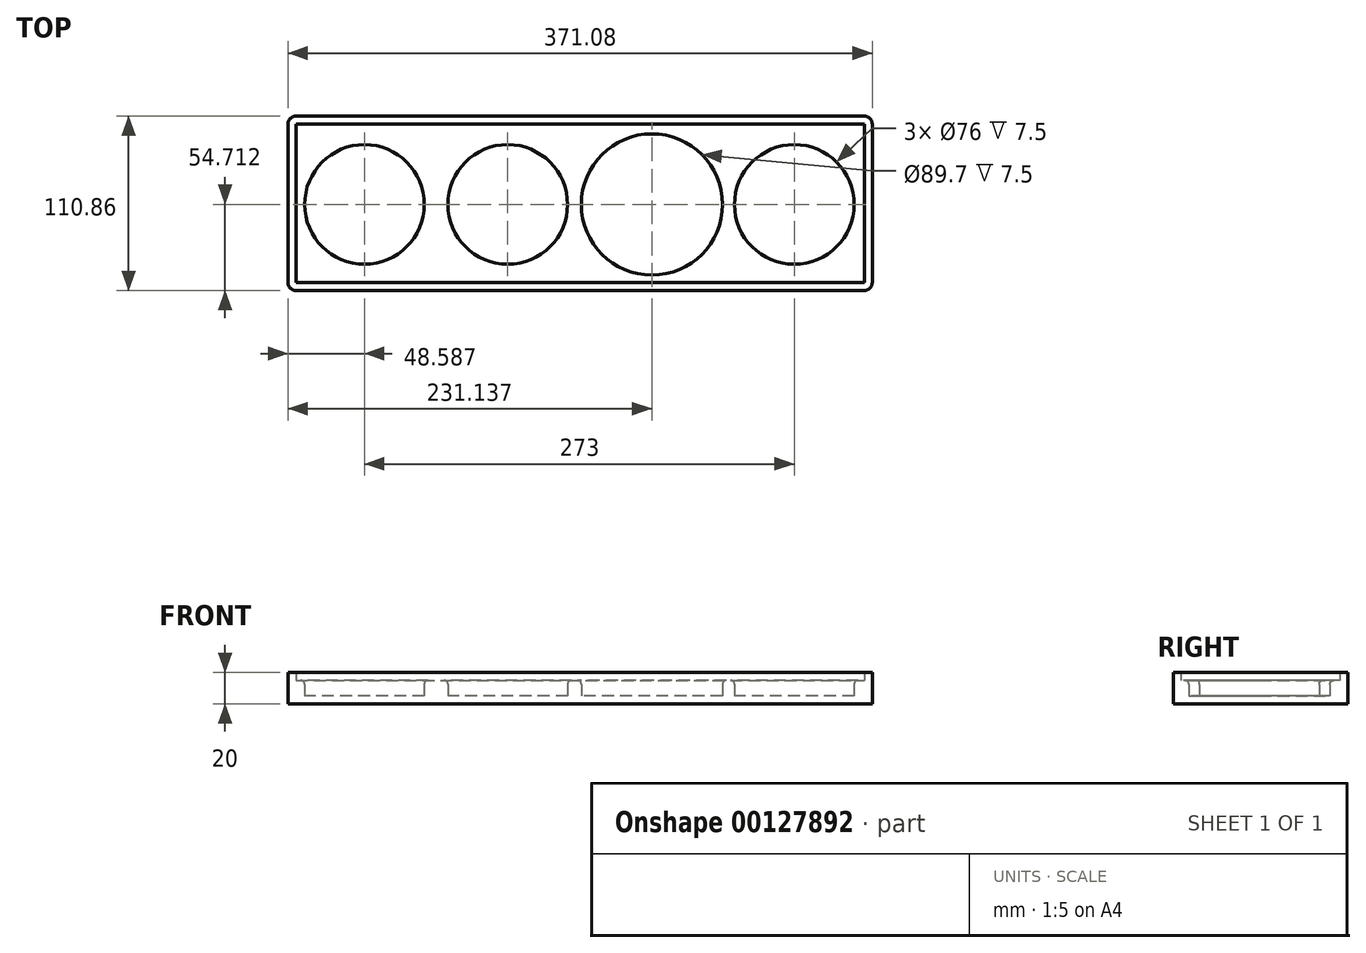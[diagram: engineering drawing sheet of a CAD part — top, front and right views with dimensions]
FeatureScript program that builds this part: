
annotation { "Feature Type Name" : "Feature", "Feature Type Description" : "" }
export const myFeature = defineFeature(function(context is Context, id is Id, definition is map)
    precondition{}
    {
        {
            var Q0;
            Q0=qCreatedBy(makeId("Top.planeOp"),FACE);
            var sketch = newSketch(context, id + "F0", { "sketchPlane" : qUnion([Q0])});
            skCircle(sketch, "E0", {"center": v(-103.8, 10.07) * mm, "radius": 38 * mm});
            skCircle(sketch, "E1.1.0.0", {"center": v(-12.8, 10.07) * mm, "radius": 38 * mm});
            skCircle(sketch, "E1.3.0.0", {"center": v(169.2, 10.07) * mm, "radius": 38 * mm});
            skLineSegment(sketch, "E1.direction1", {"start": v(-103.8, 10.07) * mm, "end": v(-12.8, 10.07) * mm, "construction": true});
            skCircle(sketch, "E2", {"center": v(78.76, 10.07) * mm, "radius": 44.85 * mm});
            skSolve(sketch);
        }
        {
            var Q0;
            Q0=makeQuery(id+"F0.imprint","IMPRINT",FACE,{"disambiguationData":[TD([[makeQuery(id+"F0.imprint","IMPRINT",EDGE,{"derivedFrom":sQuery(id+"F0.wireOp",EDGE,"E0")}),1.0]])]});
            var Q1;
            Q1=makeQuery(id+"F0.imprint","IMPRINT",FACE,{"disambiguationData":[TD([[makeQuery(id+"F0.imprint","IMPRINT",EDGE,{"derivedFrom":sQuery(id+"F0.wireOp",EDGE,"E1.1.0.0")}),1.0]])]});
            var Q2;
            Q2=makeQuery(id+"F0.imprint","IMPRINT",FACE,{"disambiguationData":[TD([[makeQuery(id+"F0.imprint","IMPRINT",EDGE,{"derivedFrom":sQuery(id+"F0.wireOp",EDGE,"E2")}),1.0]])]});
            var Q3;
            Q3=makeQuery(id+"F0.imprint","IMPRINT",FACE,{"disambiguationData":[TD([[makeQuery(id+"F0.imprint","IMPRINT",EDGE,{"derivedFrom":sQuery(id+"F0.wireOp",EDGE,"E1.3.0.0")}),1.0]])]});
            extrude(context, id + "F1", {"entities" : qUnion([Q0, Q1, Q2, Q3]), "depth" : 100 * mm});
        }
        {
            var Q0;
            Q0=qCreatedBy(makeId("Top.planeOp"),FACE);
            var sketch = newSketch(context, id + "F2", { "sketchPlane" : qUnion([Q0])});
            skLineSegment(sketch, "E3.bottom", {"start": v(-148.45, 62.29) * mm, "end": v(214.77, 62.29) * mm});
            skLineSegment(sketch, "E3.top", {"start": v(-148.45, -40.71) * mm, "end": v(214.77, -40.71) * mm});
            skLineSegment(sketch, "E3.left", {"start": v(-148.45, 62.29) * mm, "end": v(-148.45, -40.71) * mm});
            skLineSegment(sketch, "E3.right", {"start": v(214.77, 62.29) * mm, "end": v(214.77, -40.71) * mm});
            skCircle(sketch, "E4.0", {"center": v(78.76, 10.07) * mm, "radius": 44.85 * mm, "construction": true});
            skCircle(sketch, "E5.0", {"center": v(169.2, 10.07) * mm, "radius": 38 * mm, "construction": true});
            skCircle(sketch, "E6.0", {"center": v(-12.8, 10.07) * mm, "radius": 38 * mm, "construction": true});
            skCircle(sketch, "E7.0", {"center": v(-103.8, 10.07) * mm, "radius": 38 * mm, "construction": true});
            skLineSegment(sketch, "E8", {"start": v(169.2, 10.07) * mm, "end": v(214.77, 10.07) * mm, "construction": true});
            skPoint(sketch, "E8.endSnap0", {"position": v(214.77, 10.79) * mm});
            skLineSegment(sketch, "E9.0", {"start": v(-152.38, 66.22) * mm, "end": v(218.7, 66.22) * mm});
            skLineSegment(sketch, "E9.1", {"start": v(-152.38, 66.22) * mm, "end": v(-152.38, -44.64) * mm});
            skLineSegment(sketch, "E9.2", {"start": v(-152.38, -44.64) * mm, "end": v(218.7, -44.64) * mm});
            skLineSegment(sketch, "E9.3", {"start": v(218.7, 66.22) * mm, "end": v(218.7, -44.64) * mm});
            skSolve(sketch);
        }
        {
            var Q0;
            Q0=makeQuery(id+"F2.imprint","IMPRINT",FACE,{"disambiguationData":[TD([[makeQuery(id+"F2.imprint","IMPRINT",EDGE,{"derivedFrom":sQuery(id+"F2.wireOp",EDGE,"E3.bottom")}),-1.0]])]});
            var Q1;
            Q1=makeQuery(id+"F2.imprint","IMPRINT",FACE,{"disambiguationData":[TD([[makeQuery(id+"F2.imprint","IMPRINT",EDGE,{"derivedFrom":sQuery(id+"F2.wireOp",EDGE,"E3.bottom")}),1.0]])]});
            extrude(context, id + "F3", {"entities" : qUnion([Q0, Q1]), "depth" : 15 * mm});
        }
        {
            var Q0;
            Q0=makeQuery(id+"F3.opExtrude","CAP_FACE",FACE,{"disambiguationData":[OSD([sQuery(id+"F2.wireOp",EDGE,"E9.0"),sQuery(id+"F2.wireOp",EDGE,"E9.1"),sQuery(id+"F2.wireOp",EDGE,"E9.2"),sQuery(id+"F2.wireOp",EDGE,"E9.3")])],"isStart":false});
            var sketch = newSketch(context, id + "F4", { "sketchPlane" : qUnion([Q0])});
            skLineSegment(sketch, "E10.0", {"start": v(-147.38, 61.22) * mm, "end": v(213.7, 61.22) * mm});
            skLineSegment(sketch, "E10.1", {"start": v(-147.38, 61.22) * mm, "end": v(-147.38, -39.64) * mm});
            skLineSegment(sketch, "E10.2", {"start": v(-147.38, -39.64) * mm, "end": v(213.7, -39.64) * mm});
            skLineSegment(sketch, "E10.3", {"start": v(213.7, 61.22) * mm, "end": v(213.7, -39.64) * mm});
            skLineSegment(sketch, "E11.0", {"start": v(-152.38, 66.22) * mm, "end": v(218.7, 66.22) * mm});
            skLineSegment(sketch, "E11.1", {"start": v(-152.38, 66.22) * mm, "end": v(-152.38, -44.64) * mm});
            skLineSegment(sketch, "E11.2", {"start": v(-152.38, -44.64) * mm, "end": v(218.7, -44.64) * mm});
            skLineSegment(sketch, "E11.3", {"start": v(218.7, 66.22) * mm, "end": v(218.7, -44.64) * mm});
            skSolve(sketch);
        }
        {
            var Q0;
            Q0=makeQuery(id+"F4.imprint","IMPRINT",FACE,{"disambiguationData":[TD([[makeQuery(id+"F4.imprint","IMPRINT",EDGE,{"derivedFrom":sQuery(id+"F4.wireOp",EDGE,"E10.0")}),1.0]])]});
            extrude(context, id + "F5", {"entities" : qUnion([Q0]), "operationType" : NewBodyOperationType.ADD, "depth" : 5 * mm});
        }
        {
            var Q0;
            Q0=makeQuery(id+"F1.opExtrude","SWEPT_BODY",BODY,{"disambiguationData":[OSD([sQuery(id+"F0.wireOp",EDGE,"E0")])]});
            var Q1;
            Q1=makeQuery(id+"F1.opExtrude","SWEPT_BODY",BODY,{"disambiguationData":[OSD([sQuery(id+"F0.wireOp",EDGE,"E1.1.0.0")])]});
            var Q2;
            Q2=makeQuery(id+"F1.opExtrude","SWEPT_BODY",BODY,{"disambiguationData":[OSD([sQuery(id+"F0.wireOp",EDGE,"E2")])]});
            var Q3;
            Q3=makeQuery(id+"F1.opExtrude","SWEPT_BODY",BODY,{"disambiguationData":[OSD([sQuery(id+"F0.wireOp",EDGE,"E1.3.0.0")])]});
            var Q4;
            Q4=makeQuery(id+"F3.opExtrude","SWEPT_BODY",BODY,{"disambiguationData":[OSD([sQuery(id+"F2.wireOp",EDGE,"E9.0"),sQuery(id+"F2.wireOp",EDGE,"E9.1"),sQuery(id+"F2.wireOp",EDGE,"E9.2"),sQuery(id+"F2.wireOp",EDGE,"E9.3")])]});
            var Q5;
            Q5=makeQuery(id+"F1.opExtrude","CAP_FACE",FACE,{"disambiguationData":[OSD([sQuery(id+"F0.wireOp",EDGE,"E0")])],"isStart":true});
            var Q6;
            Q6=makeQuery(id+"F1.opExtrude","CAP_FACE",FACE,{"disambiguationData":[OSD([sQuery(id+"F0.wireOp",EDGE,"E1.1.0.0")])],"isStart":true});
            var Q7;
            Q7=makeQuery(id+"F1.opExtrude","CAP_FACE",FACE,{"disambiguationData":[OSD([sQuery(id+"F0.wireOp",EDGE,"E2")])],"isStart":true});
            var Q8;
            Q8=makeQuery(id+"F1.opExtrude","CAP_FACE",FACE,{"disambiguationData":[OSD([sQuery(id+"F0.wireOp",EDGE,"E1.3.0.0")])],"isStart":true});
            booleanBodies(context, id + "F6", {"operationType" : BooleanOperationType.SUBTRACTION, "tools" : qUnion([Q0, Q1, Q2, Q3]), "targets" : qUnion([Q4]), "offset" : true, "entitiesToOffset" : qUnion([Q5, Q6, Q7, Q8]), "offsetDistance" : 5 * mm, "oppositeDirection" : true});
        }
        {
            var Q0;
            Q0=makeQuery(id+"F6.tempBoolean.opBoolean","INTERSECT",EDGE,{"derivedFrom":[makeQuery(id+"F3.opExtrude","CAP_FACE",FACE,{"disambiguationData":[OSD([sQuery(id+"F2.wireOp",EDGE,"E9.0"),sQuery(id+"F2.wireOp",EDGE,"E9.1"),sQuery(id+"F2.wireOp",EDGE,"E9.2"),sQuery(id+"F2.wireOp",EDGE,"E9.3")])],"isStart":false}),makeQuery(id+"F6.offsetTempBody.opPattern","COPY",FACE,{"derivedFrom":makeQuery(id+"F1.opExtrude","SWEPT_FACE",FACE,{"disambiguationData":[OSD([sQuery(id+"F0.wireOp",EDGE,"E0")])]}),"instanceName":"1"})]});
            var Q1;
            Q1=makeQuery(id+"F6.tempBoolean.opBoolean","INTERSECT",EDGE,{"derivedFrom":[makeQuery(id+"F3.opExtrude","CAP_FACE",FACE,{"disambiguationData":[OSD([sQuery(id+"F2.wireOp",EDGE,"E9.0"),sQuery(id+"F2.wireOp",EDGE,"E9.1"),sQuery(id+"F2.wireOp",EDGE,"E9.2"),sQuery(id+"F2.wireOp",EDGE,"E9.3")])],"isStart":false}),makeQuery(id+"F6.offsetTempBody.opPattern","COPY",FACE,{"derivedFrom":makeQuery(id+"F1.opExtrude","SWEPT_FACE",FACE,{"disambiguationData":[OSD([sQuery(id+"F0.wireOp",EDGE,"E1.1.0.0")])]}),"instanceName":"1"})]});
            var Q2;
            Q2=makeQuery(id+"F6.tempBoolean.opBoolean","INTERSECT",EDGE,{"derivedFrom":[makeQuery(id+"F3.opExtrude","CAP_FACE",FACE,{"disambiguationData":[OSD([sQuery(id+"F2.wireOp",EDGE,"E9.0"),sQuery(id+"F2.wireOp",EDGE,"E9.1"),sQuery(id+"F2.wireOp",EDGE,"E9.2"),sQuery(id+"F2.wireOp",EDGE,"E9.3")])],"isStart":false}),makeQuery(id+"F6.offsetTempBody.opPattern","COPY",FACE,{"derivedFrom":makeQuery(id+"F1.opExtrude","SWEPT_FACE",FACE,{"disambiguationData":[OSD([sQuery(id+"F0.wireOp",EDGE,"E2")])]}),"instanceName":"1"})]});
            var Q3;
            Q3=makeQuery(id+"F6.tempBoolean.opBoolean","INTERSECT",EDGE,{"derivedFrom":[makeQuery(id+"F3.opExtrude","CAP_FACE",FACE,{"disambiguationData":[OSD([sQuery(id+"F2.wireOp",EDGE,"E9.0"),sQuery(id+"F2.wireOp",EDGE,"E9.1"),sQuery(id+"F2.wireOp",EDGE,"E9.2"),sQuery(id+"F2.wireOp",EDGE,"E9.3")])],"isStart":false}),makeQuery(id+"F6.offsetTempBody.opPattern","COPY",FACE,{"derivedFrom":makeQuery(id+"F1.opExtrude","SWEPT_FACE",FACE,{"disambiguationData":[OSD([sQuery(id+"F0.wireOp",EDGE,"E1.3.0.0")])]}),"instanceName":"1"})]});
            fillet(context, id + "F7", {"entities" : qUnion([Q0, Q1, Q2, Q3]), "radius" : 2.5 * mm, "tangentPropagation" : true, "allowEdgeOverflow" : false});
        }
        {
            var Q0;
            Q0=makeQuery(id+"F5.boolean.opBoolean","MERGE",EDGE,{"derivedFrom":[makeQuery(id+"F3.opExtrude","SWEPT_EDGE",EDGE,{"disambiguationData":[OSD([sQuery(id+"F2.wireOp",EDGE,"E9.1"),sQuery(id+"F2.wireOp",EDGE,"E9.2")])]}),makeQuery(id+"F5.opExtrude","SWEPT_EDGE",EDGE,{"disambiguationData":[OSD([sQuery(id+"F4.wireOp",EDGE,"E11.1"),sQuery(id+"F4.wireOp",EDGE,"E11.2")])]})]});
            var Q1;
            Q1=makeQuery(id+"F5.boolean.opBoolean","MERGE",EDGE,{"derivedFrom":[makeQuery(id+"F3.opExtrude","SWEPT_EDGE",EDGE,{"disambiguationData":[OSD([sQuery(id+"F2.wireOp",EDGE,"E9.0"),sQuery(id+"F2.wireOp",EDGE,"E9.1")])]}),makeQuery(id+"F5.opExtrude","SWEPT_EDGE",EDGE,{"disambiguationData":[OSD([sQuery(id+"F4.wireOp",EDGE,"E11.0"),sQuery(id+"F4.wireOp",EDGE,"E11.1")])]})]});
            var Q2;
            Q2=makeQuery(id+"F5.boolean.opBoolean","MERGE",EDGE,{"derivedFrom":[makeQuery(id+"F3.opExtrude","SWEPT_EDGE",EDGE,{"disambiguationData":[OSD([sQuery(id+"F2.wireOp",EDGE,"E9.2"),sQuery(id+"F2.wireOp",EDGE,"E9.3")])]}),makeQuery(id+"F5.opExtrude","SWEPT_EDGE",EDGE,{"disambiguationData":[OSD([sQuery(id+"F4.wireOp",EDGE,"E11.2"),sQuery(id+"F4.wireOp",EDGE,"E11.3")])]})]});
            var Q3;
            Q3=makeQuery(id+"F5.boolean.opBoolean","MERGE",EDGE,{"derivedFrom":[makeQuery(id+"F3.opExtrude","SWEPT_EDGE",EDGE,{"disambiguationData":[OSD([sQuery(id+"F2.wireOp",EDGE,"E9.0"),sQuery(id+"F2.wireOp",EDGE,"E9.3")])]}),makeQuery(id+"F5.opExtrude","SWEPT_EDGE",EDGE,{"disambiguationData":[OSD([sQuery(id+"F4.wireOp",EDGE,"E11.0"),sQuery(id+"F4.wireOp",EDGE,"E11.3")])]})]});
            fillet(context, id + "F8", {"entities" : qUnion([Q0, Q1, Q2, Q3]), "radius" : 5 * mm, "tangentPropagation" : true, "allowEdgeOverflow" : false});
        }
    });
